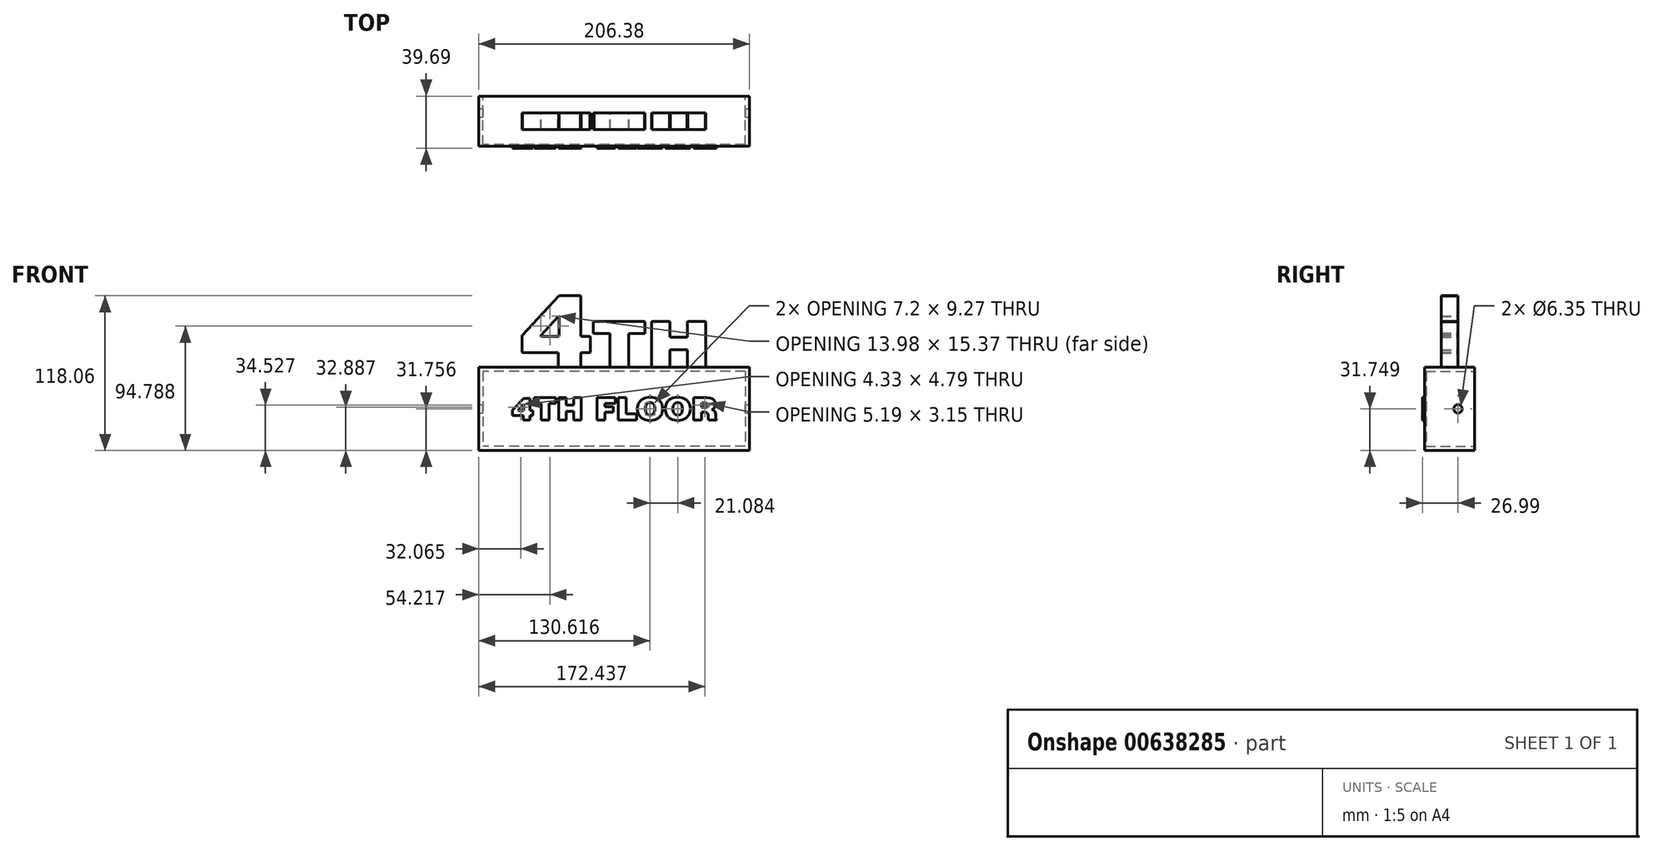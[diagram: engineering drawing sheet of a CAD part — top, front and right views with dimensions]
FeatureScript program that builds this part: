
annotation { "Feature Type Name" : "Feature", "Feature Type Description" : "" }
export const myFeature = defineFeature(function(context is Context, id is Id, definition is map)
    precondition{}
    {
        {
            var Q0;
            Q0=qCreatedBy(makeId("Front.planeOp"),FACE);
            var sketch = newSketch(context, id + "F0", { "sketchPlane" : qUnion([Q0])});
            skLineSegment(sketch, "E0", {"start": v(-55.59, 28.07) * mm, "end": v(-42.37, 28.07) * mm});
            skLineSegment(sketch, "E1", {"start": v(-42.37, 28.07) * mm, "end": v(-42.3, 28.07) * mm});
            skLineSegment(sketch, "E2", {"start": v(-42.3, 28.07) * mm, "end": v(-42.1, 28.19) * mm});
            skLineSegment(sketch, "E3", {"start": v(-42.1, 28.19) * mm, "end": v(-41.98, 28.4) * mm});
            skLineSegment(sketch, "E4", {"start": v(-41.98, 28.4) * mm, "end": v(-41.98, 28.46) * mm});
            skLineSegment(sketch, "E5", {"start": v(-41.98, 28.46) * mm, "end": v(-41.98, 43.07) * mm});
            skLineSegment(sketch, "E6", {"start": v(-41.98, 43.07) * mm, "end": v(-41.98, 43.16) * mm});
            skLineSegment(sketch, "E7", {"start": v(-41.98, 43.16) * mm, "end": v(-42.2, 43.42) * mm});
            skLineSegment(sketch, "E8", {"start": v(-42.2, 43.42) * mm, "end": v(-42.23, 43.43) * mm});
            skLineSegment(sketch, "E9", {"start": v(-42.23, 43.43) * mm, "end": v(-42.27, 43.44) * mm});
            skLineSegment(sketch, "E10", {"start": v(-42.27, 43.44) * mm, "end": v(-42.63, 43.36) * mm});
            skLineSegment(sketch, "E11", {"start": v(-42.63, 43.36) * mm, "end": v(-42.66, 43.33) * mm});
            skLineSegment(sketch, "E12", {"start": v(-42.66, 43.33) * mm, "end": v(-55.88, 28.72) * mm});
            skLineSegment(sketch, "E13", {"start": v(-55.88, 28.72) * mm, "end": v(-55.9, 28.69) * mm});
            skLineSegment(sketch, "E14", {"start": v(-55.9, 28.69) * mm, "end": v(-55.96, 28.34) * mm});
            skLineSegment(sketch, "E15", {"start": v(-55.96, 28.34) * mm, "end": v(-55.94, 28.3) * mm});
            skLineSegment(sketch, "E16", {"start": v(-55.94, 28.3) * mm, "end": v(-55.93, 28.26) * mm});
            skLineSegment(sketch, "E17", {"start": v(-55.93, 28.26) * mm, "end": v(-55.68, 28.07) * mm});
            skLineSegment(sketch, "E18", {"start": v(-55.68, 28.07) * mm, "end": v(-55.59, 28.07) * mm});
            skLineSegment(sketch, "E19", {"start": v(-42.4, 4.6) * mm, "end": v(-42.4, 15.24) * mm});
            skLineSegment(sketch, "E20", {"start": v(-42.4, 15.24) * mm, "end": v(-42.4, 15.31) * mm});
            skLineSegment(sketch, "E21", {"start": v(-42.4, 15.31) * mm, "end": v(-42.51, 15.51) * mm});
            skLineSegment(sketch, "E22", {"start": v(-42.51, 15.51) * mm, "end": v(-42.72, 15.63) * mm});
            skLineSegment(sketch, "E23", {"start": v(-42.72, 15.63) * mm, "end": v(-42.79, 15.63) * mm});
            skLineSegment(sketch, "E24", {"start": v(-42.79, 15.63) * mm, "end": v(-69.62, 15.63) * mm});
            skLineSegment(sketch, "E25", {"start": v(-69.62, 15.63) * mm, "end": v(-69.7, 15.63) * mm});
            skLineSegment(sketch, "E26", {"start": v(-69.7, 15.63) * mm, "end": v(-69.9, 15.74) * mm});
            skLineSegment(sketch, "E27", {"start": v(-69.9, 15.74) * mm, "end": v(-70.01, 15.95) * mm});
            skLineSegment(sketch, "E28", {"start": v(-70.01, 15.95) * mm, "end": v(-70.01, 16.01) * mm});
            skLineSegment(sketch, "E29", {"start": v(-70.01, 16.01) * mm, "end": v(-70.01, 28.77) * mm});
            skLineSegment(sketch, "E30", {"start": v(-70.01, 28.77) * mm, "end": v(-70.01, 28.83) * mm});
            skLineSegment(sketch, "E31", {"start": v(-70.01, 28.83) * mm, "end": v(-69.92, 29.01) * mm});
            skLineSegment(sketch, "E32", {"start": v(-69.92, 29.01) * mm, "end": v(-69.9, 29.03) * mm});
            skLineSegment(sketch, "E33", {"start": v(-69.9, 29.03) * mm, "end": v(-42.1, 58.9) * mm});
            skLineSegment(sketch, "E34", {"start": v(-42.1, 58.9) * mm, "end": v(-42.08, 58.93) * mm});
            skLineSegment(sketch, "E35", {"start": v(-42.08, 58.93) * mm, "end": v(-41.88, 59.03) * mm});
            skLineSegment(sketch, "E36", {"start": v(-41.88, 59.03) * mm, "end": v(-41.82, 59.03) * mm});
            skLineSegment(sketch, "E37", {"start": v(-41.82, 59.03) * mm, "end": v(-25.68, 59.03) * mm});
            skLineSegment(sketch, "E38", {"start": v(-25.68, 59.03) * mm, "end": v(-25.61, 59.03) * mm});
            skLineSegment(sketch, "E39", {"start": v(-25.61, 59.03) * mm, "end": v(-25.4, 58.92) * mm});
            skLineSegment(sketch, "E40", {"start": v(-25.4, 58.92) * mm, "end": v(-25.3, 58.71) * mm});
            skLineSegment(sketch, "E41", {"start": v(-25.3, 58.71) * mm, "end": v(-25.3, 58.64) * mm});
            skLineSegment(sketch, "E42", {"start": v(-25.3, 58.64) * mm, "end": v(-25.3, 28.46) * mm});
            skLineSegment(sketch, "E43", {"start": v(-25.3, 28.46) * mm, "end": v(-25.3, 28.4) * mm});
            skLineSegment(sketch, "E44", {"start": v(-25.3, 28.4) * mm, "end": v(-25.18, 28.19) * mm});
            skLineSegment(sketch, "E45", {"start": v(-25.18, 28.19) * mm, "end": v(-24.98, 28.07) * mm});
            skLineSegment(sketch, "E46", {"start": v(-24.98, 28.07) * mm, "end": v(-24.9, 28.07) * mm});
            skLineSegment(sketch, "E47", {"start": v(-24.9, 28.07) * mm, "end": v(-18.57, 28.07) * mm});
            skLineSegment(sketch, "E48", {"start": v(-18.57, 28.07) * mm, "end": v(-18.5, 28.07) * mm});
            skLineSegment(sketch, "E49", {"start": v(-18.5, 28.07) * mm, "end": v(-18.3, 27.96) * mm});
            skLineSegment(sketch, "E50", {"start": v(-18.3, 27.96) * mm, "end": v(-18.18, 27.75) * mm});
            skLineSegment(sketch, "E51", {"start": v(-18.18, 27.75) * mm, "end": v(-18.18, 27.68) * mm});
            skLineSegment(sketch, "E52", {"start": v(-18.18, 27.68) * mm, "end": v(-18.18, 16.01) * mm});
            skLineSegment(sketch, "E53", {"start": v(-18.18, 16.01) * mm, "end": v(-18.18, 15.95) * mm});
            skLineSegment(sketch, "E54", {"start": v(-18.18, 15.95) * mm, "end": v(-18.3, 15.74) * mm});
            skLineSegment(sketch, "E55", {"start": v(-18.3, 15.74) * mm, "end": v(-18.5, 15.63) * mm});
            skLineSegment(sketch, "E56", {"start": v(-18.5, 15.63) * mm, "end": v(-18.57, 15.63) * mm});
            skLineSegment(sketch, "E57", {"start": v(-18.57, 15.63) * mm, "end": v(-24.9, 15.63) * mm});
            skLineSegment(sketch, "E58", {"start": v(-24.9, 15.63) * mm, "end": v(-24.98, 15.63) * mm});
            skLineSegment(sketch, "E59", {"start": v(-24.98, 15.63) * mm, "end": v(-25.18, 15.51) * mm});
            skLineSegment(sketch, "E60", {"start": v(-25.18, 15.51) * mm, "end": v(-25.3, 15.31) * mm});
            skLineSegment(sketch, "E61", {"start": v(-25.3, 15.31) * mm, "end": v(-25.3, 15.24) * mm});
            skLineSegment(sketch, "E62", {"start": v(-25.3, 15.24) * mm, "end": v(-25.3, 4.6) * mm});
            skLineSegment(sketch, "E63", {"start": v(-25.3, 4.6) * mm, "end": v(-25.3, 4.53) * mm});
            skLineSegment(sketch, "E64", {"start": v(-25.3, 4.53) * mm, "end": v(-25.4, 4.33) * mm});
            skLineSegment(sketch, "E65", {"start": v(-25.4, 4.33) * mm, "end": v(-25.61, 4.21) * mm});
            skLineSegment(sketch, "E66", {"start": v(-25.61, 4.21) * mm, "end": v(-25.68, 4.21) * mm});
            skLineSegment(sketch, "E67", {"start": v(-25.68, 4.21) * mm, "end": v(-42.01, 4.21) * mm});
            skLineSegment(sketch, "E68", {"start": v(-42.01, 4.21) * mm, "end": v(-42.08, 4.21) * mm});
            skLineSegment(sketch, "E69", {"start": v(-42.08, 4.21) * mm, "end": v(-42.28, 4.33) * mm});
            skLineSegment(sketch, "E70", {"start": v(-42.28, 4.33) * mm, "end": v(-42.4, 4.53) * mm});
            skLineSegment(sketch, "E71", {"start": v(-42.4, 4.53) * mm, "end": v(-42.4, 4.6) * mm});
            skLineSegment(sketch, "E72", {"start": v(-3, 4.6) * mm, "end": v(-3, 29.71) * mm});
            skLineSegment(sketch, "E73", {"start": v(-3, 29.71) * mm, "end": v(-3, 29.78) * mm});
            skLineSegment(sketch, "E74", {"start": v(-3, 29.78) * mm, "end": v(-3.11, 29.98) * mm});
            skLineSegment(sketch, "E75", {"start": v(-3.11, 29.98) * mm, "end": v(-3.32, 30.1) * mm});
            skLineSegment(sketch, "E76", {"start": v(-3.32, 30.1) * mm, "end": v(-3.38, 30.1) * mm});
            skLineSegment(sketch, "E77", {"start": v(-3.38, 30.1) * mm, "end": v(-15.31, 30.1) * mm});
            skLineSegment(sketch, "E78", {"start": v(-15.31, 30.1) * mm, "end": v(-15.38, 30.1) * mm});
            skLineSegment(sketch, "E79", {"start": v(-15.38, 30.1) * mm, "end": v(-15.59, 30.21) * mm});
            skLineSegment(sketch, "E80", {"start": v(-15.59, 30.21) * mm, "end": v(-15.7, 30.42) * mm});
            skLineSegment(sketch, "E81", {"start": v(-15.7, 30.42) * mm, "end": v(-15.7, 30.48) * mm});
            skLineSegment(sketch, "E82", {"start": v(-15.7, 30.48) * mm, "end": v(-15.7, 38.97) * mm});
            skLineSegment(sketch, "E83", {"start": v(-15.7, 38.97) * mm, "end": v(-15.7, 39.04) * mm});
            skLineSegment(sketch, "E84", {"start": v(-15.7, 39.04) * mm, "end": v(-15.59, 39.25) * mm});
            skLineSegment(sketch, "E85", {"start": v(-15.59, 39.25) * mm, "end": v(-15.38, 39.36) * mm});
            skLineSegment(sketch, "E86", {"start": v(-15.38, 39.36) * mm, "end": v(-15.31, 39.36) * mm});
            skLineSegment(sketch, "E87", {"start": v(-15.31, 39.36) * mm, "end": v(23.23, 39.36) * mm});
            skLineSegment(sketch, "E88", {"start": v(23.23, 39.36) * mm, "end": v(23.3, 39.36) * mm});
            skLineSegment(sketch, "E89", {"start": v(23.3, 39.36) * mm, "end": v(23.5, 39.25) * mm});
            skLineSegment(sketch, "E90", {"start": v(23.5, 39.25) * mm, "end": v(23.61, 39.04) * mm});
            skLineSegment(sketch, "E91", {"start": v(23.61, 39.04) * mm, "end": v(23.61, 38.97) * mm});
            skLineSegment(sketch, "E92", {"start": v(23.61, 38.97) * mm, "end": v(23.61, 30.48) * mm});
            skLineSegment(sketch, "E93", {"start": v(23.61, 30.48) * mm, "end": v(23.61, 30.42) * mm});
            skLineSegment(sketch, "E94", {"start": v(23.61, 30.42) * mm, "end": v(23.5, 30.21) * mm});
            skLineSegment(sketch, "E95", {"start": v(23.5, 30.21) * mm, "end": v(23.3, 30.1) * mm});
            skLineSegment(sketch, "E96", {"start": v(23.3, 30.1) * mm, "end": v(23.23, 30.1) * mm});
            skLineSegment(sketch, "E97", {"start": v(23.23, 30.1) * mm, "end": v(11.56, 30.1) * mm});
            skLineSegment(sketch, "E98", {"start": v(11.56, 30.1) * mm, "end": v(11.5, 30.1) * mm});
            skLineSegment(sketch, "E99", {"start": v(11.5, 30.1) * mm, "end": v(11.29, 29.98) * mm});
            skLineSegment(sketch, "E100", {"start": v(11.29, 29.98) * mm, "end": v(11.18, 29.78) * mm});
            skLineSegment(sketch, "E101", {"start": v(11.18, 29.78) * mm, "end": v(11.18, 29.71) * mm});
            skLineSegment(sketch, "E102", {"start": v(11.18, 29.71) * mm, "end": v(11.18, 4.6) * mm});
            skLineSegment(sketch, "E103", {"start": v(11.18, 4.6) * mm, "end": v(11.18, 4.53) * mm});
            skLineSegment(sketch, "E104", {"start": v(11.18, 4.53) * mm, "end": v(11.06, 4.33) * mm});
            skLineSegment(sketch, "E105", {"start": v(11.06, 4.33) * mm, "end": v(10.86, 4.21) * mm});
            skLineSegment(sketch, "E106", {"start": v(10.86, 4.21) * mm, "end": v(10.8, 4.21) * mm});
            skLineSegment(sketch, "E107", {"start": v(10.8, 4.21) * mm, "end": v(-2.61, 4.21) * mm});
            skLineSegment(sketch, "E108", {"start": v(-2.61, 4.21) * mm, "end": v(-2.68, 4.21) * mm});
            skLineSegment(sketch, "E109", {"start": v(-2.68, 4.21) * mm, "end": v(-2.89, 4.33) * mm});
            skLineSegment(sketch, "E110", {"start": v(-2.89, 4.33) * mm, "end": v(-3, 4.53) * mm});
            skLineSegment(sketch, "E111", {"start": v(-3, 4.53) * mm, "end": v(-3, 4.6) * mm});
            skLineSegment(sketch, "E112", {"start": v(28.46, 4.6) * mm, "end": v(28.46, 38.97) * mm});
            skLineSegment(sketch, "E113", {"start": v(28.46, 38.97) * mm, "end": v(28.46, 39.04) * mm});
            skLineSegment(sketch, "E114", {"start": v(28.46, 39.04) * mm, "end": v(28.57, 39.25) * mm});
            skLineSegment(sketch, "E115", {"start": v(28.57, 39.25) * mm, "end": v(28.78, 39.36) * mm});
            skLineSegment(sketch, "E116", {"start": v(28.78, 39.36) * mm, "end": v(28.85, 39.36) * mm});
            skLineSegment(sketch, "E117", {"start": v(28.85, 39.36) * mm, "end": v(42.25, 39.36) * mm});
            skLineSegment(sketch, "E118", {"start": v(42.25, 39.36) * mm, "end": v(42.32, 39.36) * mm});
            skLineSegment(sketch, "E119", {"start": v(42.32, 39.36) * mm, "end": v(42.52, 39.25) * mm});
            skLineSegment(sketch, "E120", {"start": v(42.52, 39.25) * mm, "end": v(42.63, 39.04) * mm});
            skLineSegment(sketch, "E121", {"start": v(42.63, 39.04) * mm, "end": v(42.63, 38.97) * mm});
            skLineSegment(sketch, "E122", {"start": v(42.63, 38.97) * mm, "end": v(42.63, 27.81) * mm});
            skLineSegment(sketch, "E123", {"start": v(42.63, 27.81) * mm, "end": v(42.63, 27.74) * mm});
            skLineSegment(sketch, "E124", {"start": v(42.63, 27.74) * mm, "end": v(42.75, 27.54) * mm});
            skLineSegment(sketch, "E125", {"start": v(42.75, 27.54) * mm, "end": v(42.95, 27.43) * mm});
            skLineSegment(sketch, "E126", {"start": v(42.95, 27.43) * mm, "end": v(43.02, 27.43) * mm});
            skLineSegment(sketch, "E127", {"start": v(43.02, 27.43) * mm, "end": v(55.45, 27.43) * mm});
            skLineSegment(sketch, "E128", {"start": v(55.45, 27.43) * mm, "end": v(55.52, 27.43) * mm});
            skLineSegment(sketch, "E129", {"start": v(55.52, 27.43) * mm, "end": v(55.72, 27.54) * mm});
            skLineSegment(sketch, "E130", {"start": v(55.72, 27.54) * mm, "end": v(55.84, 27.74) * mm});
            skLineSegment(sketch, "E131", {"start": v(55.84, 27.74) * mm, "end": v(55.84, 27.81) * mm});
            skLineSegment(sketch, "E132", {"start": v(55.84, 27.81) * mm, "end": v(55.84, 38.97) * mm});
            skLineSegment(sketch, "E133", {"start": v(55.84, 38.97) * mm, "end": v(55.84, 39.04) * mm});
            skLineSegment(sketch, "E134", {"start": v(55.84, 39.04) * mm, "end": v(55.95, 39.25) * mm});
            skLineSegment(sketch, "E135", {"start": v(55.95, 39.25) * mm, "end": v(56.16, 39.36) * mm});
            skLineSegment(sketch, "E136", {"start": v(56.16, 39.36) * mm, "end": v(56.22, 39.36) * mm});
            skLineSegment(sketch, "E137", {"start": v(56.22, 39.36) * mm, "end": v(69.63, 39.36) * mm});
            skLineSegment(sketch, "E138", {"start": v(69.63, 39.36) * mm, "end": v(69.7, 39.36) * mm});
            skLineSegment(sketch, "E139", {"start": v(69.7, 39.36) * mm, "end": v(69.9, 39.25) * mm});
            skLineSegment(sketch, "E140", {"start": v(69.9, 39.25) * mm, "end": v(70.01, 39.04) * mm});
            skLineSegment(sketch, "E141", {"start": v(70.01, 39.04) * mm, "end": v(70.01, 38.97) * mm});
            skLineSegment(sketch, "E142", {"start": v(70.01, 38.97) * mm, "end": v(70.01, 4.6) * mm});
            skLineSegment(sketch, "E143", {"start": v(70.01, 4.6) * mm, "end": v(70.01, 4.53) * mm});
            skLineSegment(sketch, "E144", {"start": v(70.01, 4.53) * mm, "end": v(69.9, 4.33) * mm});
            skLineSegment(sketch, "E145", {"start": v(69.9, 4.33) * mm, "end": v(69.7, 4.21) * mm});
            skLineSegment(sketch, "E146", {"start": v(69.7, 4.21) * mm, "end": v(69.63, 4.21) * mm});
            skLineSegment(sketch, "E147", {"start": v(69.63, 4.21) * mm, "end": v(56.22, 4.21) * mm});
            skLineSegment(sketch, "E148", {"start": v(56.22, 4.21) * mm, "end": v(56.16, 4.21) * mm});
            skLineSegment(sketch, "E149", {"start": v(56.16, 4.21) * mm, "end": v(55.95, 4.33) * mm});
            skLineSegment(sketch, "E150", {"start": v(55.95, 4.33) * mm, "end": v(55.84, 4.53) * mm});
            skLineSegment(sketch, "E151", {"start": v(55.84, 4.53) * mm, "end": v(55.84, 4.6) * mm});
            skLineSegment(sketch, "E152", {"start": v(55.84, 4.6) * mm, "end": v(55.84, 17.44) * mm});
            skLineSegment(sketch, "E153", {"start": v(55.84, 17.44) * mm, "end": v(55.84, 17.51) * mm});
            skLineSegment(sketch, "E154", {"start": v(55.84, 17.51) * mm, "end": v(55.72, 17.72) * mm});
            skLineSegment(sketch, "E155", {"start": v(55.72, 17.72) * mm, "end": v(55.52, 17.83) * mm});
            skLineSegment(sketch, "E156", {"start": v(55.52, 17.83) * mm, "end": v(55.45, 17.83) * mm});
            skLineSegment(sketch, "E157", {"start": v(55.45, 17.83) * mm, "end": v(43.02, 17.83) * mm});
            skLineSegment(sketch, "E158", {"start": v(43.02, 17.83) * mm, "end": v(42.95, 17.83) * mm});
            skLineSegment(sketch, "E159", {"start": v(42.95, 17.83) * mm, "end": v(42.75, 17.72) * mm});
            skLineSegment(sketch, "E160", {"start": v(42.75, 17.72) * mm, "end": v(42.63, 17.51) * mm});
            skLineSegment(sketch, "E161", {"start": v(42.63, 17.51) * mm, "end": v(42.63, 17.44) * mm});
            skLineSegment(sketch, "E162", {"start": v(42.63, 17.44) * mm, "end": v(42.63, 4.6) * mm});
            skLineSegment(sketch, "E163", {"start": v(42.63, 4.6) * mm, "end": v(42.63, 4.53) * mm});
            skLineSegment(sketch, "E164", {"start": v(42.63, 4.53) * mm, "end": v(42.52, 4.33) * mm});
            skLineSegment(sketch, "E165", {"start": v(42.52, 4.33) * mm, "end": v(42.32, 4.21) * mm});
            skLineSegment(sketch, "E166", {"start": v(42.32, 4.21) * mm, "end": v(42.25, 4.21) * mm});
            skLineSegment(sketch, "E167", {"start": v(42.25, 4.21) * mm, "end": v(28.85, 4.21) * mm});
            skLineSegment(sketch, "E168", {"start": v(28.85, 4.21) * mm, "end": v(28.78, 4.21) * mm});
            skLineSegment(sketch, "E169", {"start": v(28.78, 4.21) * mm, "end": v(28.57, 4.33) * mm});
            skLineSegment(sketch, "E170", {"start": v(28.57, 4.33) * mm, "end": v(28.46, 4.53) * mm});
            skLineSegment(sketch, "E171", {"start": v(28.46, 4.53) * mm, "end": v(28.46, 4.6) * mm});
            skLineSegment(sketch, "E172", {"start": v(-103.19, 4.47) * mm, "end": v(103.19, 4.47) * mm});
            skLineSegment(sketch, "E173", {"start": v(103.19, 4.47) * mm, "end": v(103.19, -59.03) * mm});
            skLineSegment(sketch, "E174", {"start": v(103.19, -59.03) * mm, "end": v(-103.19, -59.03) * mm});
            skLineSegment(sketch, "E175", {"start": v(-103.19, -59.03) * mm, "end": v(-103.19, 4.47) * mm});
            skLineSegment(sketch, "E176", {"start": v(-73.3, -28.54) * mm, "end": v(-68.96, -28.54) * mm});
            skLineSegment(sketch, "E177", {"start": v(-68.96, -28.54) * mm, "end": v(-68.96, -23.75) * mm});
            skLineSegment(sketch, "E178", {"start": v(-68.96, -23.75) * mm, "end": v(-73.3, -28.54) * mm});
            skLineSegment(sketch, "E179", {"start": v(-69.08, -35.68) * mm, "end": v(-69.08, -32.27) * mm});
            skLineSegment(sketch, "E180", {"start": v(-69.08, -32.27) * mm, "end": v(-77.35, -32.27) * mm});
            skLineSegment(sketch, "E181", {"start": v(-77.35, -32.27) * mm, "end": v(-77.35, -28.29) * mm});
            skLineSegment(sketch, "E182", {"start": v(-77.35, -28.29) * mm, "end": v(-68.96, -19.27) * mm});
            skLineSegment(sketch, "E183", {"start": v(-68.96, -19.27) * mm, "end": v(-63.96, -19.27) * mm});
            skLineSegment(sketch, "E184", {"start": v(-63.96, -19.27) * mm, "end": v(-63.96, -28.54) * mm});
            skLineSegment(sketch, "E185", {"start": v(-63.96, -28.54) * mm, "end": v(-61.83, -28.54) * mm});
            skLineSegment(sketch, "E186", {"start": v(-61.83, -28.54) * mm, "end": v(-61.83, -32.27) * mm});
            skLineSegment(sketch, "E187", {"start": v(-61.83, -32.27) * mm, "end": v(-63.96, -32.27) * mm});
            skLineSegment(sketch, "E188", {"start": v(-63.96, -32.27) * mm, "end": v(-63.96, -35.68) * mm});
            skLineSegment(sketch, "E189", {"start": v(-63.96, -35.68) * mm, "end": v(-69.08, -35.68) * mm});
            skLineSegment(sketch, "E190", {"start": v(-55.5, -35.68) * mm, "end": v(-55.5, -23.28) * mm});
            skLineSegment(sketch, "E191", {"start": v(-55.5, -23.28) * mm, "end": v(-60.82, -23.28) * mm});
            skLineSegment(sketch, "E192", {"start": v(-60.82, -23.28) * mm, "end": v(-60.82, -18.85) * mm});
            skLineSegment(sketch, "E193", {"start": v(-60.82, -18.85) * mm, "end": v(-44.38, -18.85) * mm});
            skLineSegment(sketch, "E194", {"start": v(-44.38, -18.85) * mm, "end": v(-44.38, -23.28) * mm});
            skLineSegment(sketch, "E195", {"start": v(-44.38, -23.28) * mm, "end": v(-49.58, -23.28) * mm});
            skLineSegment(sketch, "E196", {"start": v(-49.58, -23.28) * mm, "end": v(-49.58, -35.68) * mm});
            skLineSegment(sketch, "E197", {"start": v(-49.58, -35.68) * mm, "end": v(-55.5, -35.68) * mm});
            skLineSegment(sketch, "E198", {"start": v(-42.35, -35.68) * mm, "end": v(-42.35, -18.85) * mm});
            skLineSegment(sketch, "E199", {"start": v(-42.35, -18.85) * mm, "end": v(-36.43, -18.85) * mm});
            skLineSegment(sketch, "E200", {"start": v(-36.43, -18.85) * mm, "end": v(-36.43, -24.56) * mm});
            skLineSegment(sketch, "E201", {"start": v(-36.43, -24.56) * mm, "end": v(-30.9, -24.56) * mm});
            skLineSegment(sketch, "E202", {"start": v(-30.9, -24.56) * mm, "end": v(-30.9, -18.85) * mm});
            skLineSegment(sketch, "E203", {"start": v(-30.9, -18.85) * mm, "end": v(-24.98, -18.85) * mm});
            skLineSegment(sketch, "E204", {"start": v(-24.98, -18.85) * mm, "end": v(-24.98, -35.68) * mm});
            skLineSegment(sketch, "E205", {"start": v(-24.98, -35.68) * mm, "end": v(-30.9, -35.68) * mm});
            skLineSegment(sketch, "E206", {"start": v(-30.9, -35.68) * mm, "end": v(-30.9, -29.16) * mm});
            skLineSegment(sketch, "E207", {"start": v(-30.9, -29.16) * mm, "end": v(-36.43, -29.16) * mm});
            skLineSegment(sketch, "E208", {"start": v(-36.43, -29.16) * mm, "end": v(-36.43, -35.68) * mm});
            skLineSegment(sketch, "E209", {"start": v(-36.43, -35.68) * mm, "end": v(-42.35, -35.68) * mm});
            skLineSegment(sketch, "E210", {"start": v(-13.05, -35.68) * mm, "end": v(-13.05, -18.85) * mm});
            skLineSegment(sketch, "E211", {"start": v(-13.05, -18.85) * mm, "end": v(0.9, -18.85) * mm});
            skLineSegment(sketch, "E212", {"start": v(0.9, -18.85) * mm, "end": v(0.9, -23.09) * mm});
            skLineSegment(sketch, "E213", {"start": v(0.9, -23.09) * mm, "end": v(-7.13, -23.09) * mm});
            skLineSegment(sketch, "E214", {"start": v(-7.13, -23.09) * mm, "end": v(-7.13, -25.7) * mm});
            skLineSegment(sketch, "E215", {"start": v(-7.13, -25.7) * mm, "end": v(-0.74, -25.7) * mm});
            skLineSegment(sketch, "E216", {"start": v(-0.74, -25.7) * mm, "end": v(-0.74, -29.76) * mm});
            skLineSegment(sketch, "E217", {"start": v(-0.74, -29.76) * mm, "end": v(-7.13, -29.76) * mm});
            skLineSegment(sketch, "E218", {"start": v(-7.13, -29.76) * mm, "end": v(-7.13, -35.68) * mm});
            skLineSegment(sketch, "E219", {"start": v(-7.13, -35.68) * mm, "end": v(-13.05, -35.68) * mm});
            skLineSegment(sketch, "E220", {"start": v(3.16, -35.68) * mm, "end": v(3.16, -18.85) * mm});
            skLineSegment(sketch, "E221", {"start": v(3.16, -18.85) * mm, "end": v(9.08, -18.85) * mm});
            skLineSegment(sketch, "E222", {"start": v(9.08, -18.85) * mm, "end": v(9.08, -31.21) * mm});
            skLineSegment(sketch, "E223", {"start": v(9.08, -31.21) * mm, "end": v(17.14, -31.21) * mm});
            skLineSegment(sketch, "E224", {"start": v(17.14, -31.21) * mm, "end": v(17.14, -35.68) * mm});
            skLineSegment(sketch, "E225", {"start": v(17.14, -35.68) * mm, "end": v(3.16, -35.68) * mm});
            skLineSegment(sketch, "E226", {"start": v(23.82, -27.28) * mm, "end": v(23.82, -27.8) * mm});
            skLineSegment(sketch, "E227", {"start": v(23.82, -27.8) * mm, "end": v(24.04, -29.35) * mm});
            skLineSegment(sketch, "E228", {"start": v(24.04, -29.35) * mm, "end": v(24.55, -30.6) * mm});
            skLineSegment(sketch, "E229", {"start": v(24.55, -30.6) * mm, "end": v(24.7, -30.8) * mm});
            skLineSegment(sketch, "E230", {"start": v(24.7, -30.8) * mm, "end": v(24.85, -30.98) * mm});
            skLineSegment(sketch, "E231", {"start": v(24.85, -30.98) * mm, "end": v(25.83, -31.63) * mm});
            skLineSegment(sketch, "E232", {"start": v(25.83, -31.63) * mm, "end": v(27.04, -31.9) * mm});
            skLineSegment(sketch, "E233", {"start": v(27.04, -31.9) * mm, "end": v(27.44, -31.9) * mm});
            skLineSegment(sketch, "E234", {"start": v(27.44, -31.9) * mm, "end": v(27.85, -31.9) * mm});
            skLineSegment(sketch, "E235", {"start": v(27.85, -31.9) * mm, "end": v(29.05, -31.63) * mm});
            skLineSegment(sketch, "E236", {"start": v(29.05, -31.63) * mm, "end": v(30.02, -30.98) * mm});
            skLineSegment(sketch, "E237", {"start": v(30.02, -30.98) * mm, "end": v(30.16, -30.8) * mm});
            skLineSegment(sketch, "E238", {"start": v(30.16, -30.8) * mm, "end": v(30.3, -30.6) * mm});
            skLineSegment(sketch, "E239", {"start": v(30.3, -30.6) * mm, "end": v(30.81, -29.36) * mm});
            skLineSegment(sketch, "E240", {"start": v(30.81, -29.36) * mm, "end": v(31.03, -27.8) * mm});
            skLineSegment(sketch, "E241", {"start": v(31.03, -27.8) * mm, "end": v(31.03, -27.28) * mm});
            skLineSegment(sketch, "E242", {"start": v(31.03, -27.28) * mm, "end": v(31.03, -26.76) * mm});
            skLineSegment(sketch, "E243", {"start": v(31.03, -26.76) * mm, "end": v(30.81, -25.2) * mm});
            skLineSegment(sketch, "E244", {"start": v(30.81, -25.2) * mm, "end": v(30.3, -23.94) * mm});
            skLineSegment(sketch, "E245", {"start": v(30.3, -23.94) * mm, "end": v(30.16, -23.75) * mm});
            skLineSegment(sketch, "E246", {"start": v(30.16, -23.75) * mm, "end": v(30.02, -23.57) * mm});
            skLineSegment(sketch, "E247", {"start": v(30.02, -23.57) * mm, "end": v(29.05, -22.92) * mm});
            skLineSegment(sketch, "E248", {"start": v(29.05, -22.92) * mm, "end": v(27.85, -22.64) * mm});
            skLineSegment(sketch, "E249", {"start": v(27.85, -22.64) * mm, "end": v(27.44, -22.64) * mm});
            skLineSegment(sketch, "E250", {"start": v(27.44, -22.64) * mm, "end": v(27.04, -22.64) * mm});
            skLineSegment(sketch, "E251", {"start": v(27.04, -22.64) * mm, "end": v(25.83, -22.92) * mm});
            skLineSegment(sketch, "E252", {"start": v(25.83, -22.92) * mm, "end": v(24.85, -23.57) * mm});
            skLineSegment(sketch, "E253", {"start": v(24.85, -23.57) * mm, "end": v(24.7, -23.76) * mm});
            skLineSegment(sketch, "E254", {"start": v(24.7, -23.76) * mm, "end": v(24.55, -23.94) * mm});
            skLineSegment(sketch, "E255", {"start": v(24.55, -23.94) * mm, "end": v(24.04, -25.2) * mm});
            skLineSegment(sketch, "E256", {"start": v(24.04, -25.2) * mm, "end": v(23.82, -26.76) * mm});
            skLineSegment(sketch, "E257", {"start": v(23.82, -26.76) * mm, "end": v(23.82, -27.28) * mm});
            skLineSegment(sketch, "E258", {"start": v(17.85, -27.28) * mm, "end": v(17.85, -26.36) * mm});
            skLineSegment(sketch, "E259", {"start": v(17.85, -26.36) * mm, "end": v(18.5, -23.6) * mm});
            skLineSegment(sketch, "E260", {"start": v(18.5, -23.6) * mm, "end": v(20, -21.18) * mm});
            skLineSegment(sketch, "E261", {"start": v(20, -21.18) * mm, "end": v(20.42, -20.79) * mm});
            skLineSegment(sketch, "E262", {"start": v(20.42, -20.79) * mm, "end": v(20.85, -20.39) * mm});
            skLineSegment(sketch, "E263", {"start": v(20.85, -20.39) * mm, "end": v(23.47, -19) * mm});
            skLineSegment(sketch, "E264", {"start": v(23.47, -19) * mm, "end": v(26.45, -18.4) * mm});
            skLineSegment(sketch, "E265", {"start": v(26.45, -18.4) * mm, "end": v(27.44, -18.4) * mm});
            skLineSegment(sketch, "E266", {"start": v(27.44, -18.4) * mm, "end": v(28.44, -18.4) * mm});
            skLineSegment(sketch, "E267", {"start": v(28.44, -18.4) * mm, "end": v(31.41, -19) * mm});
            skLineSegment(sketch, "E268", {"start": v(31.41, -19) * mm, "end": v(34.02, -20.39) * mm});
            skLineSegment(sketch, "E269", {"start": v(34.02, -20.39) * mm, "end": v(34.44, -20.79) * mm});
            skLineSegment(sketch, "E270", {"start": v(34.44, -20.79) * mm, "end": v(34.87, -21.18) * mm});
            skLineSegment(sketch, "E271", {"start": v(34.87, -21.18) * mm, "end": v(36.37, -23.6) * mm});
            skLineSegment(sketch, "E272", {"start": v(36.37, -23.6) * mm, "end": v(37.01, -26.36) * mm});
            skLineSegment(sketch, "E273", {"start": v(37.01, -26.36) * mm, "end": v(37.01, -27.28) * mm});
            skLineSegment(sketch, "E274", {"start": v(37.01, -27.28) * mm, "end": v(37.01, -28.2) * mm});
            skLineSegment(sketch, "E275", {"start": v(37.01, -28.2) * mm, "end": v(36.37, -30.95) * mm});
            skLineSegment(sketch, "E276", {"start": v(36.37, -30.95) * mm, "end": v(34.87, -33.37) * mm});
            skLineSegment(sketch, "E277", {"start": v(34.87, -33.37) * mm, "end": v(34.44, -33.77) * mm});
            skLineSegment(sketch, "E278", {"start": v(34.44, -33.77) * mm, "end": v(34.02, -34.16) * mm});
            skLineSegment(sketch, "E279", {"start": v(34.02, -34.16) * mm, "end": v(31.41, -35.55) * mm});
            skLineSegment(sketch, "E280", {"start": v(31.41, -35.55) * mm, "end": v(28.44, -36.15) * mm});
            skLineSegment(sketch, "E281", {"start": v(28.44, -36.15) * mm, "end": v(27.44, -36.15) * mm});
            skLineSegment(sketch, "E282", {"start": v(27.44, -36.15) * mm, "end": v(26.45, -36.15) * mm});
            skLineSegment(sketch, "E283", {"start": v(26.45, -36.15) * mm, "end": v(23.47, -35.55) * mm});
            skLineSegment(sketch, "E284", {"start": v(23.47, -35.55) * mm, "end": v(20.85, -34.16) * mm});
            skLineSegment(sketch, "E285", {"start": v(20.85, -34.16) * mm, "end": v(20.42, -33.77) * mm});
            skLineSegment(sketch, "E286", {"start": v(20.42, -33.77) * mm, "end": v(20, -33.37) * mm});
            skLineSegment(sketch, "E287", {"start": v(20, -33.37) * mm, "end": v(18.5, -30.95) * mm});
            skLineSegment(sketch, "E288", {"start": v(18.5, -30.95) * mm, "end": v(17.85, -28.2) * mm});
            skLineSegment(sketch, "E289", {"start": v(17.85, -28.2) * mm, "end": v(17.85, -27.28) * mm});
            skLineSegment(sketch, "E290", {"start": v(44.9, -27.28) * mm, "end": v(44.9, -27.8) * mm});
            skLineSegment(sketch, "E291", {"start": v(44.9, -27.8) * mm, "end": v(45.13, -29.35) * mm});
            skLineSegment(sketch, "E292", {"start": v(45.13, -29.35) * mm, "end": v(45.64, -30.6) * mm});
            skLineSegment(sketch, "E293", {"start": v(45.64, -30.6) * mm, "end": v(45.78, -30.8) * mm});
            skLineSegment(sketch, "E294", {"start": v(45.78, -30.8) * mm, "end": v(45.93, -30.98) * mm});
            skLineSegment(sketch, "E295", {"start": v(45.93, -30.98) * mm, "end": v(46.9, -31.63) * mm});
            skLineSegment(sketch, "E296", {"start": v(46.9, -31.63) * mm, "end": v(48.12, -31.9) * mm});
            skLineSegment(sketch, "E297", {"start": v(48.12, -31.9) * mm, "end": v(48.53, -31.9) * mm});
            skLineSegment(sketch, "E298", {"start": v(48.53, -31.9) * mm, "end": v(48.93, -31.9) * mm});
            skLineSegment(sketch, "E299", {"start": v(48.93, -31.9) * mm, "end": v(50.13, -31.63) * mm});
            skLineSegment(sketch, "E300", {"start": v(50.13, -31.63) * mm, "end": v(51.1, -30.98) * mm});
            skLineSegment(sketch, "E301", {"start": v(51.1, -30.98) * mm, "end": v(51.25, -30.8) * mm});
            skLineSegment(sketch, "E302", {"start": v(51.25, -30.8) * mm, "end": v(51.4, -30.6) * mm});
            skLineSegment(sketch, "E303", {"start": v(51.4, -30.6) * mm, "end": v(51.9, -29.36) * mm});
            skLineSegment(sketch, "E304", {"start": v(51.9, -29.36) * mm, "end": v(52.11, -27.8) * mm});
            skLineSegment(sketch, "E305", {"start": v(52.11, -27.8) * mm, "end": v(52.11, -27.28) * mm});
            skLineSegment(sketch, "E306", {"start": v(52.11, -27.28) * mm, "end": v(52.11, -26.76) * mm});
            skLineSegment(sketch, "E307", {"start": v(52.11, -26.76) * mm, "end": v(51.9, -25.2) * mm});
            skLineSegment(sketch, "E308", {"start": v(51.9, -25.2) * mm, "end": v(51.4, -23.94) * mm});
            skLineSegment(sketch, "E309", {"start": v(51.4, -23.94) * mm, "end": v(51.25, -23.75) * mm});
            skLineSegment(sketch, "E310", {"start": v(51.25, -23.75) * mm, "end": v(51.1, -23.57) * mm});
            skLineSegment(sketch, "E311", {"start": v(51.1, -23.57) * mm, "end": v(50.13, -22.92) * mm});
            skLineSegment(sketch, "E312", {"start": v(50.13, -22.92) * mm, "end": v(48.93, -22.64) * mm});
            skLineSegment(sketch, "E313", {"start": v(48.93, -22.64) * mm, "end": v(48.53, -22.64) * mm});
            skLineSegment(sketch, "E314", {"start": v(48.53, -22.64) * mm, "end": v(48.12, -22.64) * mm});
            skLineSegment(sketch, "E315", {"start": v(48.12, -22.64) * mm, "end": v(46.9, -22.92) * mm});
            skLineSegment(sketch, "E316", {"start": v(46.9, -22.92) * mm, "end": v(45.93, -23.57) * mm});
            skLineSegment(sketch, "E317", {"start": v(45.93, -23.57) * mm, "end": v(45.78, -23.76) * mm});
            skLineSegment(sketch, "E318", {"start": v(45.78, -23.76) * mm, "end": v(45.64, -23.94) * mm});
            skLineSegment(sketch, "E319", {"start": v(45.64, -23.94) * mm, "end": v(45.13, -25.2) * mm});
            skLineSegment(sketch, "E320", {"start": v(45.13, -25.2) * mm, "end": v(44.9, -26.76) * mm});
            skLineSegment(sketch, "E321", {"start": v(44.9, -26.76) * mm, "end": v(44.9, -27.28) * mm});
            skLineSegment(sketch, "E322", {"start": v(38.93, -27.28) * mm, "end": v(38.93, -26.36) * mm});
            skLineSegment(sketch, "E323", {"start": v(38.93, -26.36) * mm, "end": v(39.58, -23.6) * mm});
            skLineSegment(sketch, "E324", {"start": v(39.58, -23.6) * mm, "end": v(41.08, -21.18) * mm});
            skLineSegment(sketch, "E325", {"start": v(41.08, -21.18) * mm, "end": v(41.5, -20.79) * mm});
            skLineSegment(sketch, "E326", {"start": v(41.5, -20.79) * mm, "end": v(41.94, -20.39) * mm});
            skLineSegment(sketch, "E327", {"start": v(41.94, -20.39) * mm, "end": v(44.55, -19) * mm});
            skLineSegment(sketch, "E328", {"start": v(44.55, -19) * mm, "end": v(47.53, -18.4) * mm});
            skLineSegment(sketch, "E329", {"start": v(47.53, -18.4) * mm, "end": v(48.53, -18.4) * mm});
            skLineSegment(sketch, "E330", {"start": v(48.53, -18.4) * mm, "end": v(49.52, -18.4) * mm});
            skLineSegment(sketch, "E331", {"start": v(49.52, -18.4) * mm, "end": v(52.5, -19) * mm});
            skLineSegment(sketch, "E332", {"start": v(52.5, -19) * mm, "end": v(55.1, -20.39) * mm});
            skLineSegment(sketch, "E333", {"start": v(55.1, -20.39) * mm, "end": v(55.53, -20.79) * mm});
            skLineSegment(sketch, "E334", {"start": v(55.53, -20.79) * mm, "end": v(55.96, -21.18) * mm});
            skLineSegment(sketch, "E335", {"start": v(55.96, -21.18) * mm, "end": v(57.45, -23.6) * mm});
            skLineSegment(sketch, "E336", {"start": v(57.45, -23.6) * mm, "end": v(58.1, -26.36) * mm});
            skLineSegment(sketch, "E337", {"start": v(58.1, -26.36) * mm, "end": v(58.1, -27.28) * mm});
            skLineSegment(sketch, "E338", {"start": v(58.1, -27.28) * mm, "end": v(58.1, -28.2) * mm});
            skLineSegment(sketch, "E339", {"start": v(58.1, -28.2) * mm, "end": v(57.45, -30.95) * mm});
            skLineSegment(sketch, "E340", {"start": v(57.45, -30.95) * mm, "end": v(55.96, -33.37) * mm});
            skLineSegment(sketch, "E341", {"start": v(55.96, -33.37) * mm, "end": v(55.53, -33.77) * mm});
            skLineSegment(sketch, "E342", {"start": v(55.53, -33.77) * mm, "end": v(55.1, -34.16) * mm});
            skLineSegment(sketch, "E343", {"start": v(55.1, -34.16) * mm, "end": v(52.5, -35.55) * mm});
            skLineSegment(sketch, "E344", {"start": v(52.5, -35.55) * mm, "end": v(49.52, -36.15) * mm});
            skLineSegment(sketch, "E345", {"start": v(49.52, -36.15) * mm, "end": v(48.53, -36.15) * mm});
            skLineSegment(sketch, "E346", {"start": v(48.53, -36.15) * mm, "end": v(47.53, -36.15) * mm});
            skLineSegment(sketch, "E347", {"start": v(47.53, -36.15) * mm, "end": v(44.55, -35.55) * mm});
            skLineSegment(sketch, "E348", {"start": v(44.55, -35.55) * mm, "end": v(41.94, -34.16) * mm});
            skLineSegment(sketch, "E349", {"start": v(41.94, -34.16) * mm, "end": v(41.5, -33.77) * mm});
            skLineSegment(sketch, "E350", {"start": v(41.5, -33.77) * mm, "end": v(41.08, -33.37) * mm});
            skLineSegment(sketch, "E351", {"start": v(41.08, -33.37) * mm, "end": v(39.58, -30.95) * mm});
            skLineSegment(sketch, "E352", {"start": v(39.58, -30.95) * mm, "end": v(38.93, -28.2) * mm});
            skLineSegment(sketch, "E353", {"start": v(38.93, -28.2) * mm, "end": v(38.93, -27.28) * mm});
            skLineSegment(sketch, "E354", {"start": v(66.65, -26.08) * mm, "end": v(69.35, -26.08) * mm});
            skLineSegment(sketch, "E355", {"start": v(69.35, -26.08) * mm, "end": v(69.65, -26.08) * mm});
            skLineSegment(sketch, "E356", {"start": v(69.65, -26.08) * mm, "end": v(70.54, -26) * mm});
            skLineSegment(sketch, "E357", {"start": v(70.54, -26) * mm, "end": v(71.21, -25.79) * mm});
            skLineSegment(sketch, "E358", {"start": v(71.21, -25.79) * mm, "end": v(71.3, -25.73) * mm});
            skLineSegment(sketch, "E359", {"start": v(71.3, -25.73) * mm, "end": v(71.4, -25.67) * mm});
            skLineSegment(sketch, "E360", {"start": v(71.4, -25.67) * mm, "end": v(71.7, -25.25) * mm});
            skLineSegment(sketch, "E361", {"start": v(71.7, -25.25) * mm, "end": v(71.84, -24.7) * mm});
            skLineSegment(sketch, "E362", {"start": v(71.84, -24.7) * mm, "end": v(71.84, -24.52) * mm});
            skLineSegment(sketch, "E363", {"start": v(71.84, -24.52) * mm, "end": v(71.84, -24.33) * mm});
            skLineSegment(sketch, "E364", {"start": v(71.84, -24.33) * mm, "end": v(71.7, -23.76) * mm});
            skLineSegment(sketch, "E365", {"start": v(71.7, -23.76) * mm, "end": v(71.4, -23.33) * mm});
            skLineSegment(sketch, "E366", {"start": v(71.4, -23.33) * mm, "end": v(71.3, -23.27) * mm});
            skLineSegment(sketch, "E367", {"start": v(71.3, -23.27) * mm, "end": v(71.21, -23.22) * mm});
            skLineSegment(sketch, "E368", {"start": v(71.21, -23.22) * mm, "end": v(70.5, -23.01) * mm});
            skLineSegment(sketch, "E369", {"start": v(70.5, -23.01) * mm, "end": v(69.52, -22.93) * mm});
            skLineSegment(sketch, "E370", {"start": v(69.52, -22.93) * mm, "end": v(69.2, -22.93) * mm});
            skLineSegment(sketch, "E371", {"start": v(69.2, -22.93) * mm, "end": v(66.65, -22.93) * mm});
            skLineSegment(sketch, "E372", {"start": v(66.65, -22.93) * mm, "end": v(66.65, -26.08) * mm});
            skLineSegment(sketch, "E373", {"start": v(60.8, -35.68) * mm, "end": v(60.8, -18.84) * mm});
            skLineSegment(sketch, "E374", {"start": v(60.8, -18.84) * mm, "end": v(69.63, -18.84) * mm});
            skLineSegment(sketch, "E375", {"start": v(69.63, -18.84) * mm, "end": v(70.52, -18.84) * mm});
            skLineSegment(sketch, "E376", {"start": v(70.52, -18.84) * mm, "end": v(73.19, -19.13) * mm});
            skLineSegment(sketch, "E377", {"start": v(73.19, -19.13) * mm, "end": v(75.26, -19.79) * mm});
            skLineSegment(sketch, "E378", {"start": v(75.26, -19.79) * mm, "end": v(75.55, -19.98) * mm});
            skLineSegment(sketch, "E379", {"start": v(75.55, -19.98) * mm, "end": v(75.76, -20.11) * mm});
            skLineSegment(sketch, "E380", {"start": v(75.76, -20.11) * mm, "end": v(76.33, -20.63) * mm});
            skLineSegment(sketch, "E381", {"start": v(76.33, -20.63) * mm, "end": v(76.88, -21.47) * mm});
            skLineSegment(sketch, "E382", {"start": v(76.88, -21.47) * mm, "end": v(77.21, -22.5) * mm});
            skLineSegment(sketch, "E383", {"start": v(77.21, -22.5) * mm, "end": v(77.33, -23.4) * mm});
            skLineSegment(sketch, "E384", {"start": v(77.33, -23.4) * mm, "end": v(77.33, -23.7) * mm});
            skLineSegment(sketch, "E385", {"start": v(77.33, -23.7) * mm, "end": v(77.33, -24.04) * mm});
            skLineSegment(sketch, "E386", {"start": v(77.33, -24.04) * mm, "end": v(77.14, -25.1) * mm});
            skLineSegment(sketch, "E387", {"start": v(77.14, -25.1) * mm, "end": v(76.72, -26.08) * mm});
            skLineSegment(sketch, "E388", {"start": v(76.72, -26.08) * mm, "end": v(76.6, -26.25) * mm});
            skLineSegment(sketch, "E389", {"start": v(76.6, -26.25) * mm, "end": v(76.48, -26.42) * mm});
            skLineSegment(sketch, "E390", {"start": v(76.48, -26.42) * mm, "end": v(75.67, -27.16) * mm});
            skLineSegment(sketch, "E391", {"start": v(75.67, -27.16) * mm, "end": v(74.6, -27.76) * mm});
            skLineSegment(sketch, "E392", {"start": v(74.6, -27.76) * mm, "end": v(74.36, -27.86) * mm});
            skLineSegment(sketch, "E393", {"start": v(74.36, -27.86) * mm, "end": v(74.61, -27.91) * mm});
            skLineSegment(sketch, "E394", {"start": v(74.61, -27.91) * mm, "end": v(75.69, -28.3) * mm});
            skLineSegment(sketch, "E395", {"start": v(75.69, -28.3) * mm, "end": v(76.48, -28.9) * mm});
            skLineSegment(sketch, "E396", {"start": v(76.48, -28.9) * mm, "end": v(76.6, -29.04) * mm});
            skLineSegment(sketch, "E397", {"start": v(76.6, -29.04) * mm, "end": v(76.71, -29.18) * mm});
            skLineSegment(sketch, "E398", {"start": v(76.71, -29.18) * mm, "end": v(77.14, -30.11) * mm});
            skLineSegment(sketch, "E399", {"start": v(77.14, -30.11) * mm, "end": v(77.34, -31.32) * mm});
            skLineSegment(sketch, "E400", {"start": v(77.34, -31.32) * mm, "end": v(77.35, -31.6) * mm});
            skLineSegment(sketch, "E401", {"start": v(77.35, -31.6) * mm, "end": v(77.45, -33.95) * mm});
            skLineSegment(sketch, "E402", {"start": v(77.45, -33.95) * mm, "end": v(77.45, -33.96) * mm});
            skLineSegment(sketch, "E403", {"start": v(77.45, -33.96) * mm, "end": v(77.46, -34) * mm});
            skLineSegment(sketch, "E404", {"start": v(77.46, -34) * mm, "end": v(77.46, -34) * mm});
            skLineSegment(sketch, "E405", {"start": v(77.46, -34) * mm, "end": v(77.47, -34.17) * mm});
            skLineSegment(sketch, "E406", {"start": v(77.47, -34.17) * mm, "end": v(77.61, -34.77) * mm});
            skLineSegment(sketch, "E407", {"start": v(77.61, -34.77) * mm, "end": v(77.9, -35.05) * mm});
            skLineSegment(sketch, "E408", {"start": v(77.9, -35.05) * mm, "end": v(77.99, -35.06) * mm});
            skLineSegment(sketch, "E409", {"start": v(77.99, -35.06) * mm, "end": v(77.99, -35.68) * mm});
            skLineSegment(sketch, "E410", {"start": v(77.99, -35.68) * mm, "end": v(72.01, -35.68) * mm});
            skLineSegment(sketch, "E411", {"start": v(72.01, -35.68) * mm, "end": v(71.99, -35.58) * mm});
            skLineSegment(sketch, "E412", {"start": v(71.99, -35.58) * mm, "end": v(71.78, -34.7) * mm});
            skLineSegment(sketch, "E413", {"start": v(71.78, -34.7) * mm, "end": v(71.77, -34.63) * mm});
            skLineSegment(sketch, "E414", {"start": v(71.77, -34.63) * mm, "end": v(71.76, -34.55) * mm});
            skLineSegment(sketch, "E415", {"start": v(71.76, -34.55) * mm, "end": v(71.69, -34.08) * mm});
            skLineSegment(sketch, "E416", {"start": v(71.69, -34.08) * mm, "end": v(71.69, -33.92) * mm});
            skLineSegment(sketch, "E417", {"start": v(71.69, -33.92) * mm, "end": v(71.69, -32.24) * mm});
            skLineSegment(sketch, "E418", {"start": v(71.69, -32.24) * mm, "end": v(71.69, -31.96) * mm});
            skLineSegment(sketch, "E419", {"start": v(71.69, -31.96) * mm, "end": v(71.55, -31.13) * mm});
            skLineSegment(sketch, "E420", {"start": v(71.55, -31.13) * mm, "end": v(71.22, -30.5) * mm});
            skLineSegment(sketch, "E421", {"start": v(71.22, -30.5) * mm, "end": v(71.13, -30.4) * mm});
            skLineSegment(sketch, "E422", {"start": v(71.13, -30.4) * mm, "end": v(71.03, -30.32) * mm});
            skLineSegment(sketch, "E423", {"start": v(71.03, -30.32) * mm, "end": v(70.35, -30) * mm});
            skLineSegment(sketch, "E424", {"start": v(70.35, -30) * mm, "end": v(69.47, -29.88) * mm});
            skLineSegment(sketch, "E425", {"start": v(69.47, -29.88) * mm, "end": v(69.17, -29.88) * mm});
            skLineSegment(sketch, "E426", {"start": v(69.17, -29.88) * mm, "end": v(66.65, -29.88) * mm});
            skLineSegment(sketch, "E427", {"start": v(66.65, -29.88) * mm, "end": v(66.65, -35.68) * mm});
            skLineSegment(sketch, "E428", {"start": v(66.65, -35.68) * mm, "end": v(60.8, -35.68) * mm});
            skSolve(sketch);
        }
        {
            var Q0;
            {var subQ0=sQuery(id+"F0.wireOp",EDGE,"E65");Q0=makeQuery(id+"F0.imprint","IMPRINT",FACE,{"disambiguationData":[TD([[makeQuery(id+"F0.imprint","IMPRINT",EDGE,{"derivedFrom":subQ0}),-1.0]])]});}
            var Q1;
            {var subQ0=sQuery(id+"F0.wireOp",EDGE,"E105");Q1=makeQuery(id+"F0.imprint","IMPRINT",FACE,{"disambiguationData":[TD([[makeQuery(id+"F0.imprint","IMPRINT",EDGE,{"derivedFrom":subQ0}),-1.0]])]});}
            var Q2;
            {var subQ0=sQuery(id+"F0.wireOp",EDGE,"E145");Q2=makeQuery(id+"F0.imprint","IMPRINT",FACE,{"disambiguationData":[TD([[makeQuery(id+"F0.imprint","IMPRINT",EDGE,{"derivedFrom":subQ0}),-1.0]])]});}
            var Q3;
            {var subQ5=sQuery(id+"F0.wireOp",EDGE,"E165");Q3=makeQuery(id+"F0.imprint","IMPRINT",FACE,{"disambiguationData":[TD([[makeQuery(id+"F0.imprint","IMPRINT",EDGE,{"derivedFrom":subQ5}),-1.0]])]});}
            var Q4;
            {var subQ24=sQuery(id+"F0.wireOp",EDGE,"E65");Q4=makeQuery(id+"F0.imprint","IMPRINT",FACE,{"disambiguationData":[TD([[makeQuery(id+"F0.imprint","IMPRINT",EDGE,{"derivedFrom":subQ24}),1.0]])]});}
            var Q5;
            Q5=makeQuery(id+"F0.imprint","IMPRINT",FACE,{"disambiguationData":[TD([[makeQuery(id+"F0.imprint","IMPRINT",EDGE,{"derivedFrom":sQuery(id+"F0.wireOp",EDGE,"E176")}),1.0]])]});
            var Q6;
            Q6=makeQuery(id+"F0.imprint","IMPRINT",FACE,{"disambiguationData":[TD([[makeQuery(id+"F0.imprint","IMPRINT",EDGE,{"derivedFrom":sQuery(id+"F0.wireOp",EDGE,"E176")}),-1.0]])]});
            var Q7;
            Q7=makeQuery(id+"F0.imprint","IMPRINT",FACE,{"disambiguationData":[TD([[makeQuery(id+"F0.imprint","IMPRINT",EDGE,{"derivedFrom":sQuery(id+"F0.wireOp",EDGE,"E190")}),-1.0]])]});
            var Q8;
            Q8=makeQuery(id+"F0.imprint","IMPRINT",FACE,{"disambiguationData":[TD([[makeQuery(id+"F0.imprint","IMPRINT",EDGE,{"derivedFrom":sQuery(id+"F0.wireOp",EDGE,"E198")}),-1.0]])]});
            var Q9;
            Q9=makeQuery(id+"F0.imprint","IMPRINT",FACE,{"disambiguationData":[TD([[makeQuery(id+"F0.imprint","IMPRINT",EDGE,{"derivedFrom":sQuery(id+"F0.wireOp",EDGE,"E210")}),-1.0]])]});
            var Q10;
            Q10=makeQuery(id+"F0.imprint","IMPRINT",FACE,{"disambiguationData":[TD([[makeQuery(id+"F0.imprint","IMPRINT",EDGE,{"derivedFrom":sQuery(id+"F0.wireOp",EDGE,"E220")}),-1.0]])]});
            var Q11;
            Q11=makeQuery(id+"F0.imprint","IMPRINT",FACE,{"disambiguationData":[TD([[makeQuery(id+"F0.imprint","IMPRINT",EDGE,{"derivedFrom":sQuery(id+"F0.wireOp",EDGE,"E226")}),-1.0]])]});
            var Q12;
            Q12=makeQuery(id+"F0.imprint","IMPRINT",FACE,{"disambiguationData":[TD([[makeQuery(id+"F0.imprint","IMPRINT",EDGE,{"derivedFrom":sQuery(id+"F0.wireOp",EDGE,"E226")}),1.0]])]});
            var Q13;
            Q13=makeQuery(id+"F0.imprint","IMPRINT",FACE,{"disambiguationData":[TD([[makeQuery(id+"F0.imprint","IMPRINT",EDGE,{"derivedFrom":sQuery(id+"F0.wireOp",EDGE,"E290")}),-1.0]])]});
            var Q14;
            Q14=makeQuery(id+"F0.imprint","IMPRINT",FACE,{"disambiguationData":[TD([[makeQuery(id+"F0.imprint","IMPRINT",EDGE,{"derivedFrom":sQuery(id+"F0.wireOp",EDGE,"E290")}),1.0]])]});
            var Q15;
            Q15=makeQuery(id+"F0.imprint","IMPRINT",FACE,{"disambiguationData":[TD([[makeQuery(id+"F0.imprint","IMPRINT",EDGE,{"derivedFrom":sQuery(id+"F0.wireOp",EDGE,"E354")}),1.0]])]});
            var Q16;
            Q16=makeQuery(id+"F0.imprint","IMPRINT",FACE,{"disambiguationData":[TD([[makeQuery(id+"F0.imprint","IMPRINT",EDGE,{"derivedFrom":sQuery(id+"F0.wireOp",EDGE,"E354")}),-1.0]])]});
            extrude(context, id + "F1", {"entities" : qUnion([Q0, Q1, Q2, Q3, Q4, Q5, Q6, Q7, Q8, Q9, Q10, Q11, Q12, Q13, Q14, Q15, Q16]), "depth" : 19.05 * mm, "offsetDistance" : 25.4 * mm, "hasSecondDirection" : true, "secondDirectionOppositeDirection" : true, "secondDirectionDepth" : 19.05 * mm});
        }
        {
            var Q0;
            Q0=makeQuery(id+"F0.imprint","IMPRINT",FACE,{"disambiguationData":[TD([[makeQuery(id+"F0.imprint","IMPRINT",EDGE,{"derivedFrom":sQuery(id+"F0.wireOp",EDGE,"E0")}),-1.0]])]});
            var Q1;
            Q1=makeQuery(id+"F0.imprint","IMPRINT",FACE,{"disambiguationData":[TD([[makeQuery(id+"F0.imprint","IMPRINT",EDGE,{"derivedFrom":sQuery(id+"F0.wireOp",EDGE,"E72")}),-1.0]])]});
            var Q2;
            Q2=makeQuery(id+"F0.imprint","IMPRINT",FACE,{"disambiguationData":[TD([[makeQuery(id+"F0.imprint","IMPRINT",EDGE,{"derivedFrom":sQuery(id+"F0.wireOp",EDGE,"E112")}),-1.0]])]});
            extrude(context, id + "F2", {"entities" : qUnion([Q0, Q1, Q2]), "depth" : 6.35 * mm, "offsetDistance" : 25.4 * mm, "hasSecondDirection" : true, "secondDirectionOppositeDirection" : true, "secondDirectionDepth" : 6.35 * mm});
        }
        {
            var Q0;
            Q0=makeQuery(id+"F0.imprint","IMPRINT",FACE,{"disambiguationData":[TD([[makeQuery(id+"F0.imprint","IMPRINT",EDGE,{"derivedFrom":sQuery(id+"F0.wireOp",EDGE,"E176")}),-1.0]])]});
            var Q1;
            Q1=makeQuery(id+"F0.imprint","IMPRINT",FACE,{"disambiguationData":[TD([[makeQuery(id+"F0.imprint","IMPRINT",EDGE,{"derivedFrom":sQuery(id+"F0.wireOp",EDGE,"E190")}),-1.0]])]});
            var Q2;
            Q2=makeQuery(id+"F0.imprint","IMPRINT",FACE,{"disambiguationData":[TD([[makeQuery(id+"F0.imprint","IMPRINT",EDGE,{"derivedFrom":sQuery(id+"F0.wireOp",EDGE,"E198")}),-1.0]])]});
            var Q3;
            Q3=makeQuery(id+"F0.imprint","IMPRINT",FACE,{"disambiguationData":[TD([[makeQuery(id+"F0.imprint","IMPRINT",EDGE,{"derivedFrom":sQuery(id+"F0.wireOp",EDGE,"E210")}),-1.0]])]});
            var Q4;
            Q4=makeQuery(id+"F0.imprint","IMPRINT",FACE,{"disambiguationData":[TD([[makeQuery(id+"F0.imprint","IMPRINT",EDGE,{"derivedFrom":sQuery(id+"F0.wireOp",EDGE,"E220")}),-1.0]])]});
            var Q5;
            Q5=makeQuery(id+"F0.imprint","IMPRINT",FACE,{"disambiguationData":[TD([[makeQuery(id+"F0.imprint","IMPRINT",EDGE,{"derivedFrom":sQuery(id+"F0.wireOp",EDGE,"E226")}),-1.0]])]});
            var Q6;
            Q6=makeQuery(id+"F0.imprint","IMPRINT",FACE,{"disambiguationData":[TD([[makeQuery(id+"F0.imprint","IMPRINT",EDGE,{"derivedFrom":sQuery(id+"F0.wireOp",EDGE,"E290")}),-1.0]])]});
            var Q7;
            Q7=makeQuery(id+"F0.imprint","IMPRINT",FACE,{"disambiguationData":[TD([[makeQuery(id+"F0.imprint","IMPRINT",EDGE,{"derivedFrom":sQuery(id+"F0.wireOp",EDGE,"E354")}),-1.0]])]});
            extrude(context, id + "F3", {"entities" : qUnion([Q0, Q1, Q2, Q3, Q4, Q5, Q6, Q7]), "depth" : 20.64 * mm, "offsetDistance" : 25.4 * mm});
        }
        {
            var Q0;
            Q0=makeQuery(id+"F1.opExtrude","CAP_FACE",FACE,{"disambiguationData":[OSD([sQuery(id+"F0.wireOp",EDGE,"E172"),sQuery(id+"F0.wireOp",EDGE,"E173"),sQuery(id+"F0.wireOp",EDGE,"E174"),sQuery(id+"F0.wireOp",EDGE,"E175")])],"isStart":true});
            var sketch = newSketch(context, id + "F4", { "sketchPlane" : qUnion([Q0])});
            skLineSegment(sketch, "E429.bottom", {"start": v(-100.01, 1.3) * mm, "end": v(100.01, 1.3) * mm});
            skLineSegment(sketch, "E429.top", {"start": v(-100.01, -55.86) * mm, "end": v(100.01, -55.86) * mm});
            skLineSegment(sketch, "E429.left", {"start": v(-100.01, 1.3) * mm, "end": v(-100.01, -55.86) * mm});
            skLineSegment(sketch, "E429.right", {"start": v(100.01, 1.3) * mm, "end": v(100.01, -55.86) * mm});
            skSolve(sketch);
        }
        {
            var Q0;
            Q0=makeQuery(id+"F4.imprint","IMPRINT",FACE,{"disambiguationData":[TD([[makeQuery(id+"F4.imprint","IMPRINT",EDGE,{"derivedFrom":sQuery(id+"F4.wireOp",EDGE,"E429.bottom")}),-1.0]])]});
            extrude(context, id + "F5", {"entities" : qUnion([Q0]), "operationType" : NewBodyOperationType.REMOVE, "oppositeDirection" : true, "depth" : 37.47 * mm, "offsetDistance" : 25.4 * mm});
        }
        {
            var Q0;
            {var subQ0=sQuery(id+"F4.wireOp",EDGE,"E429.bottom");var subQ1=sQuery(id+"F4.wireOp",EDGE,"E429.right");var subQ2=sQuery(id+"F4.wireOp",EDGE,"E429.top");var subQ3=sQuery(id+"F4.wireOp",EDGE,"E429.left");Q0=makeQuery(id+"F5.boolean.opBoolean","COPY",FACE,{"disambiguationData":[TD([makeQuery(id+"F5.opExtrude","SWEPT_FACE",FACE,{"disambiguationData":[OSD([subQ0])]})])],"derivedFrom":makeQuery(id+"F5.opExtrude","CAP_FACE",FACE,{"disambiguationData":[OSD([subQ0,subQ2,subQ3,subQ1])],"isStart":false})});}
            var sketch = newSketch(context, id + "F6", { "sketchPlane" : qUnion([Q0])});
            skSolve(sketch);
        }
        {
            var Q0;
            Q0=makeQuery(id+"F6.imprint","IMPRINT",FACE,{"disambiguationData":[TD([[makeQuery(id+"F6.imprint","IMPRINT",EDGE,{"derivedFrom":makeQuery(id+"F5.boolean.opBoolean","COPY",EDGE,{"derivedFrom":makeQuery(id+"F5.opExtrude","CAP_EDGE",EDGE,{"disambiguationData":[OSD([sQuery(id+"F4.wireOp",EDGE,"E429.bottom")])],"isStart":false})})}),-1.0]])]});
            extrude(context, id + "F7", {"entities" : qUnion([Q0]), "depth" : 0.64 * mm, "offsetDistance" : 25.4 * mm});
        }
        {
            var Q0;
            Q0=makeQuery(id+"F1.opExtrude","SWEPT_FACE",FACE,{"disambiguationData":[OSD([sQuery(id+"F0.wireOp",EDGE,"E173")])]});
            var sketch = newSketch(context, id + "F8", { "sketchPlane" : qUnion([Q0])});
            skCircle(sketch, "E430", {"center": v(6.35, -27.28) * mm, "radius": 3.18 * mm});
            skLineSegment(sketch, "E431", {"start": v(19.05, 4.47) * mm, "end": v(-19.05, 4.47) * mm});
            skSolve(sketch);
        }
        {
            var Q0;
            Q0=makeQuery(id+"F8.imprint","IMPRINT",FACE,{"disambiguationData":[TD([[makeQuery(id+"F8.imprint","IMPRINT",EDGE,{"derivedFrom":sQuery(id+"F8.wireOp",EDGE,"E430")}),1.0]])]});
            extrude(context, id + "F9", {"entities" : qUnion([Q0]), "operationType" : NewBodyOperationType.REMOVE, "endBound" : BoundingType.THROUGH_ALL, "oppositeDirection" : true, "depth" : 22.86 * mm, "offsetDistance" : 25.4 * mm});
        }
    });
